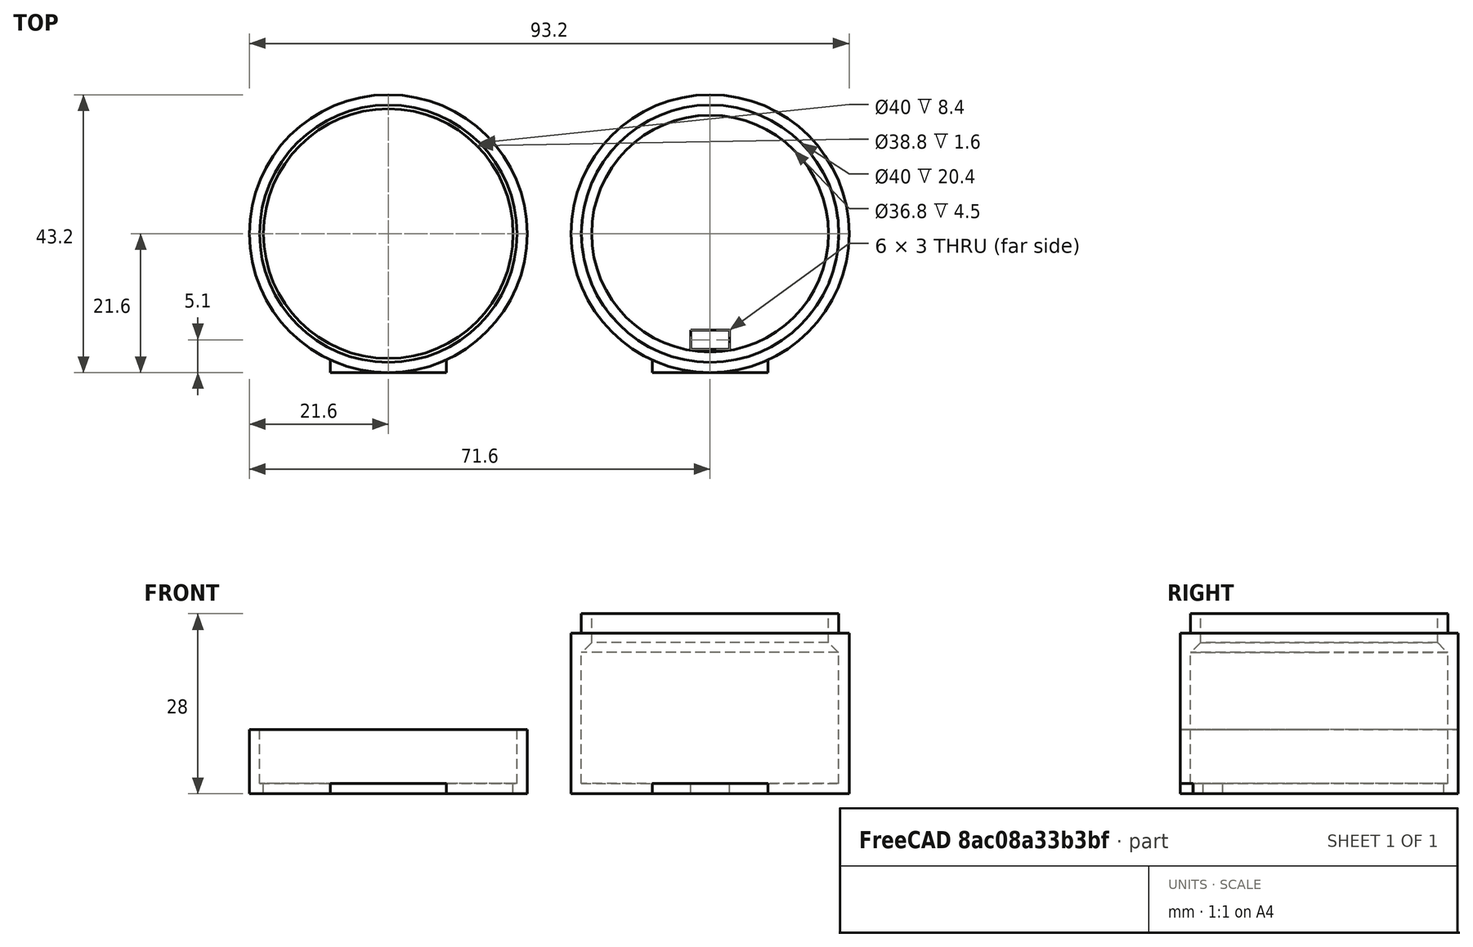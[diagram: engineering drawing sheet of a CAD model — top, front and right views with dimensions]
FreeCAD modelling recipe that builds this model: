
FCSTD DOCUMENT  (FreeCAD 0.16R)
Label: Speaker_40mm
License: All rights reserved
LicenseURL: http://en.wikipedia.org/wiki/All_rights_reserved
objects: Part::Cylinder×7, Part::Cut×5, Part::Box×3, Part::MultiFuse×3, Part::Chamfer×1
note: 19 computed .brp shape members not serialized (recipe doc carries the construction recipe); baked Part::Feature solids carry a one-line shape summary decoded from their .brp

FEATURE [Part::Cylinder] Cylinder  label="Zylinder"
  Angle = 360
  Height = 10
  Radius = 19.4
FEATURE [Part::Cylinder] Cylinder001  label="Zylinder001"
  Angle = 360
  Height = 10
  Radius = 21.6
FEATURE [Part::Cylinder] Cylinder002  label="Zylinder002"
  Angle = 360
  Height = 10
  Placement = pos=(0,0,1.6) rot=(0,0,1;0rad)
  Radius = 20
FEATURE [Part::Cut] Cut
  Base = -> Cylinder001
  Tool = -> Cylinder002
FEATURE [Part::Cut] Cut001
  Base = -> Cut
  Tool = -> Cylinder
FEATURE [Part::Box] Box  label="Würfel"
  Height = 1.6
  Length = 18
  Placement = pos=(-9,-21.6,0) rot=(0,0,1;0rad)
  Width = 2.1
FEATURE [Part::MultiFuse] Fusion
  Shapes = -> [Cut001,Box]
FEATURE [Part::Cylinder] Cylinder003  label="Zylinder003"
  Angle = 360
  Height = 25
  Placement = pos=(50,0,0) rot=(0,0,1;0rad)
  Radius = 21.6
FEATURE [Part::Cylinder] Cylinder004  label="Zylinder004"
  Angle = 360
  Height = 25
  Placement = pos=(50,0,1.6) rot=(0,0,1;0rad)
  Radius = 20
FEATURE [Part::Cut] Cut002
  Base = -> Cylinder003
  Tool = -> Cylinder004
FEATURE [Part::Box] Box001  label="Würfel001"
  Height = 1.6
  Length = 18
  Placement = pos=(41,-21.6,0) rot=(0,0,1;0rad)
  Width = 2.1
FEATURE [Part::Box] Box002  label="Würfel002"
  Height = 10
  Length = 6
  Placement = pos=(47,-18,0) rot=(0,0,1;0rad)
  Width = 3
FEATURE [Part::Cut] Cut003
  Base = -> Cut002
  Tool = -> Box002
FEATURE [Part::Cylinder] Cylinder005  label="Zylinder005"
  Angle = 360
  Height = 6
  Placement = pos=(100,0,0) rot=(0,0,1;0rad)
  Radius = 20
FEATURE [Part::Cylinder] Cylinder006  label="Zylinder006"
  Angle = 360
  Height = 6
  Placement = pos=(100,0,0) rot=(0,0,1;0rad)
  Radius = 18.4
FEATURE [Part::Cut] Cut004
  Base = -> Cylinder005
  Tool = -> Cylinder006
FEATURE [Part::Chamfer] Chamfer
  Base = -> Cut004
  Edges = 1 edges r=1.5: [Edge5]
  Placement = pos=(-50,0,22) rot=(0,0,1;0rad)
FEATURE [Part::MultiFuse] Fusion001
  Shapes = -> [Cut003,Chamfer,Box001]
FEATURE [Part::MultiFuse] Fusion002
  Shapes = -> [Fusion,Fusion001]
